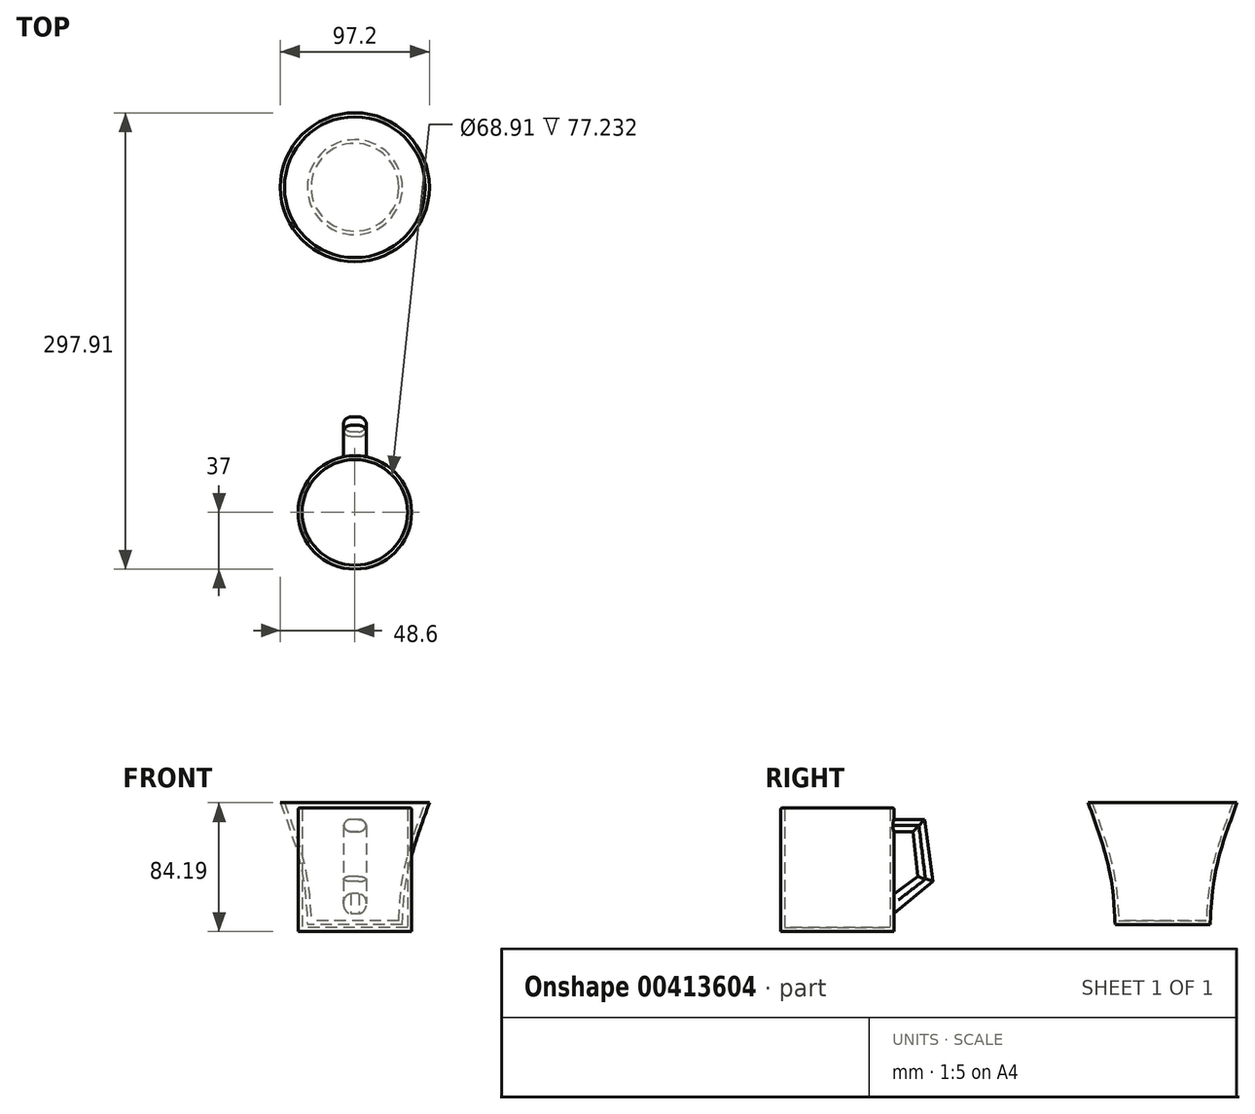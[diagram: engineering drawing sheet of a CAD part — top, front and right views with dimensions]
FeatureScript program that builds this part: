
annotation { "Feature Type Name" : "Feature", "Feature Type Description" : "" }
export const myFeature = defineFeature(function(context is Context, id is Id, definition is map)
    precondition{}
    {
        {
            var Q0;
            Q0=qCreatedBy(makeId("Top.planeOp"),FACE);
            var sketch = newSketch(context, id + "F0", { "sketchPlane" : qUnion([Q0])});
            skCircle(sketch, "E0", {"center": v(0, 0) * mm, "radius": 37 * mm});
            skSolve(sketch);
        }
        {
            var Q0;
            Q0 = qSketchRegion(id + "F0", true);
            extrude(context, id + "F1", {"entities" : qUnion([Q0]), "depth" : 80.77 * mm});
        }
        {
            var Q0;
            Q0=makeQuery(id+"F1.opExtrude","CAP_FACE",FACE,{"disambiguationData":[OSD([sQuery(id+"F0.wireOp",EDGE,"E0")])],"isStart":false});
            shell(context, id + "F2", {"entities" : qUnion([Q0]), "thickness" : 2.54 * mm});
        }
        {
            var Q0;
            {var subQ0=sQuery(id+"F0.wireOp",EDGE,"E0");Q0=makeQuery(id+"F2.opShell","OFFSET_EDGE",EDGE,{"disambiguationData":[OSD([subQ0]),TDD([makeQuery(id+"F1.opExtrude","CAP_EDGE",EDGE,{"disambiguationData":[OSD([subQ0])],"isStart":false})])]});}
            var Q1;
            Q1=makeQuery(id+"F1.opExtrude","CAP_EDGE",EDGE,{"disambiguationData":[OSD([sQuery(id+"F0.wireOp",EDGE,"E0")])],"isStart":false});
            fillet(context, id + "F3", {"entities" : qUnion([Q0, Q1]), "radius" : 1 * mm, "tangentPropagation" : true, "allowEdgeOverflow" : false});
        }
        {
            var Q0;
            Q0=qCreatedBy(makeId("Right.planeOp"),FACE);
            var sketch = newSketch(context, id + "F4", { "sketchPlane" : qUnion([Q0])});
            skLineSegment(sketch, "E1", {"start": v(36.28, 73.3) * mm, "end": v(56.88, 73.3) * mm});
            skLineSegment(sketch, "E2", {"start": v(56.88, 73.3) * mm, "end": v(62.41, 32.7) * mm});
            skLineSegment(sketch, "E3", {"start": v(62.41, 32.7) * mm, "end": v(36.9, 11.8) * mm});
            skLineSegment(sketch, "E4", {"start": v(36.9, 11.8) * mm, "end": v(36.9, 24.71) * mm});
            skLineSegment(sketch, "E5", {"start": v(36.9, 24.71) * mm, "end": v(52.57, 36.1) * mm});
            skLineSegment(sketch, "E6", {"start": v(52.57, 36.1) * mm, "end": v(49.5, 65.3) * mm});
            skLineSegment(sketch, "E7", {"start": v(49.5, 65.3) * mm, "end": v(36.28, 65.3) * mm});
            skLineSegment(sketch, "E8", {"start": v(36.28, 65.3) * mm, "end": v(36.28, 73.3) * mm});
            skSolve(sketch);
        }
        {
            var Q0;
            Q0 = qSketchRegion(id + "F4", true);
            extrude(context, id + "F5", {"entities" : qUnion([Q0]), "operationType" : NewBodyOperationType.ADD, "endBound" : BoundingType.SYMMETRIC, "depth" : 15 * mm});
        }
        {
            var Q0;
            Q0=makeQuery(id+"F5.opExtrude","CAP_EDGE",EDGE,{"disambiguationData":[OSD([sQuery(id+"F4.wireOp",EDGE,"E2")])],"isStart":false});
            var Q1;
            Q1=makeQuery(id+"F5.opExtrude","CAP_EDGE",EDGE,{"disambiguationData":[OSD([sQuery(id+"F4.wireOp",EDGE,"E1")])],"isStart":false});
            var Q2;
            Q2=makeQuery(id+"F5.opExtrude","CAP_EDGE",EDGE,{"disambiguationData":[OSD([sQuery(id+"F4.wireOp",EDGE,"E3")])],"isStart":false});
            var Q3;
            Q3=makeQuery(id+"F5.opExtrude","CAP_EDGE",EDGE,{"disambiguationData":[OSD([sQuery(id+"F4.wireOp",EDGE,"E5")])],"isStart":false});
            var Q4;
            Q4=makeQuery(id+"F5.opExtrude","CAP_EDGE",EDGE,{"disambiguationData":[OSD([sQuery(id+"F4.wireOp",EDGE,"E6")])],"isStart":false});
            var Q5;
            Q5=makeQuery(id+"F5.opExtrude","CAP_EDGE",EDGE,{"disambiguationData":[OSD([sQuery(id+"F4.wireOp",EDGE,"E7")])],"isStart":false});
            var Q6;
            Q6=makeQuery(id+"F5.opExtrude","CAP_EDGE",EDGE,{"disambiguationData":[OSD([sQuery(id+"F4.wireOp",EDGE,"E1")])],"isStart":true});
            var Q7;
            Q7=makeQuery(id+"F5.opExtrude","CAP_EDGE",EDGE,{"disambiguationData":[OSD([sQuery(id+"F4.wireOp",EDGE,"E7")])],"isStart":true});
            var Q8;
            Q8=makeQuery(id+"F5.opExtrude","CAP_EDGE",EDGE,{"disambiguationData":[OSD([sQuery(id+"F4.wireOp",EDGE,"E2")])],"isStart":true});
            var Q9;
            Q9=makeQuery(id+"F5.opExtrude","CAP_EDGE",EDGE,{"disambiguationData":[OSD([sQuery(id+"F4.wireOp",EDGE,"E6")])],"isStart":true});
            var Q10;
            Q10=makeQuery(id+"F5.opExtrude","CAP_EDGE",EDGE,{"disambiguationData":[OSD([sQuery(id+"F4.wireOp",EDGE,"E5")])],"isStart":true});
            var Q11;
            Q11=makeQuery(id+"F5.opExtrude","CAP_EDGE",EDGE,{"disambiguationData":[OSD([sQuery(id+"F4.wireOp",EDGE,"E3")])],"isStart":true});
            fillet(context, id + "F6", {"entities" : qUnion([Q0, Q1, Q2, Q3, Q4, Q5, Q6, Q7, Q8, Q9, Q10, Q11]), "radius" : 5 * mm, "tangentPropagation" : true, "allowEdgeOverflow" : false});
        }
        {
            var Q0;
            Q0=qCreatedBy(makeId("Right.planeOp"),FACE);
            var sketch = newSketch(context, id + "F7", { "sketchPlane" : qUnion([Q0])});
            skLineSegment(sketch, "E9", {"start": v(212.3, 85.17) * mm, "end": v(212.3, 4.51) * mm});
            skLineSegment(sketch, "E10", {"start": v(212.3, 4.51) * mm, "end": v(181.28, 4.51) * mm});
            skFitSpline(sketch, "E11", {"points": [v(181.28, 4.51) * mm, v(177.66, 39.67) * mm, v(163.7, 84.14) * mm], "startDerivative": vector(-3.5, 73.75) * mm, "endDerivative": vector(-31.02, 85.24) * mm});
            skLineSegment(sketch, "E12", {"start": v(163.7, 84.14) * mm, "end": v(212.3, 85.17) * mm});
            skSolve(sketch);
        }
        {
            var Q0;
            Q0=makeQuery(id+"F7.imprint","IMPRINT",FACE,{"disambiguationData":[TD([[makeQuery(id+"F7.imprint","IMPRINT",EDGE,{"derivedFrom":sQuery(id+"F7.wireOp",EDGE,"E9")}),-1.0]])]});
            var Q1;
            Q1=sQuery(id+"F7.wireOp",EDGE,"E9");
            revolve(context, id + "F8", {"entities" : qUnion([Q0]), "axis" : qUnion([Q1]), "revolveType" : RevolveType.FULL});
        }
        {
            var Q0;
            Q0=makeQuery(id+"F8.opRevolve","SWEPT_FACE",FACE,{"disambiguationData":[OSD([sQuery(id+"F7.wireOp",EDGE,"E12")])]});
            shell(context, id + "F9", {"entities" : qUnion([Q0]), "thickness" : 2.5 * mm});
        }
    });
